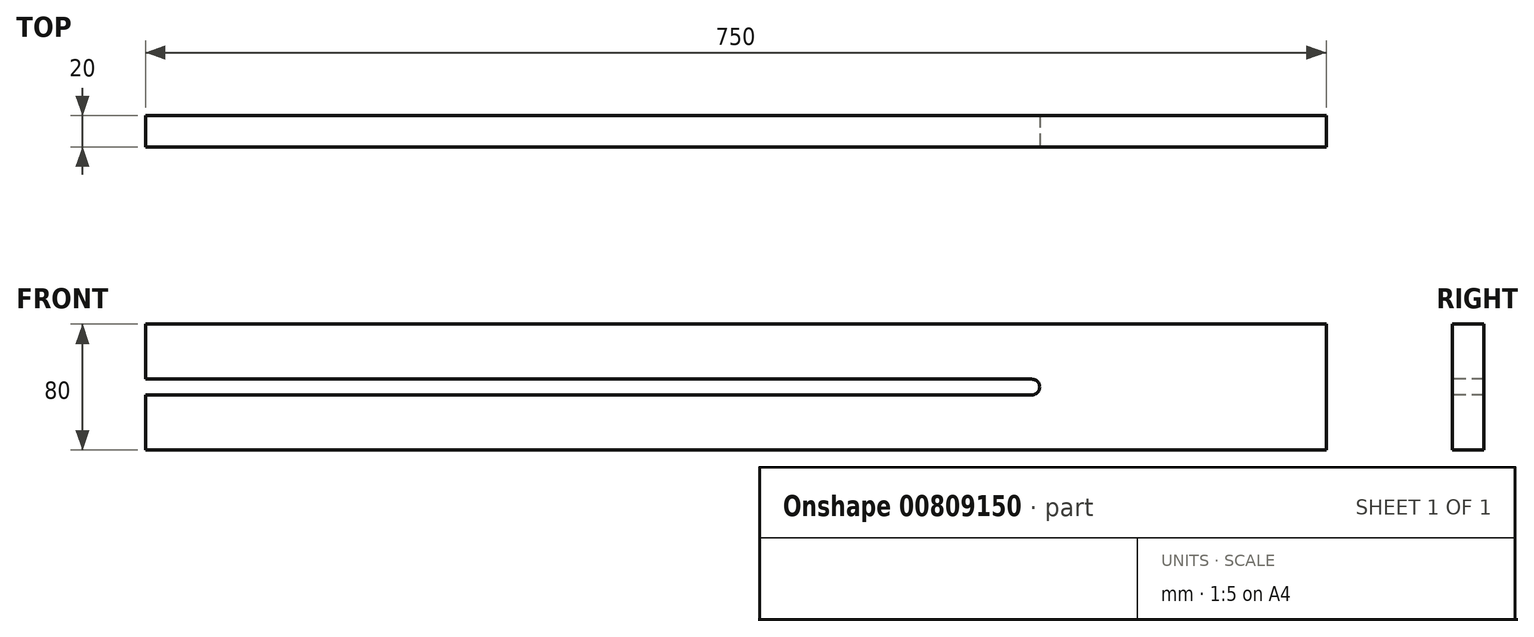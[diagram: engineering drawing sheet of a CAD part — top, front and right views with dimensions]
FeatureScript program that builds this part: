
annotation { "Feature Type Name" : "Feature", "Feature Type Description" : "" }
export const myFeature = defineFeature(function(context is Context, id is Id, definition is map)
    precondition{}
    {
        {
            var Q0;
            Q0=qCreatedBy(makeId("Front.planeOp"),FACE);
            var sketch = newSketch(context, id + "F0", { "sketchPlane" : qUnion([Q0])});
            skLineSegment(sketch, "E0.bottom", {"start": v(375, -40) * mm, "end": v(-375, -40) * mm});
            skLineSegment(sketch, "E0.top", {"start": v(375, 40) * mm, "end": v(-375, 40) * mm});
            skLineSegment(sketch, "E0.left", {"start": v(375, -40) * mm, "end": v(375, 40) * mm});
            skLineSegment(sketch, "E0.right", {"start": v(-375, -40) * mm, "end": v(-375, 40) * mm});
            skPoint(sketch, "E0.middle", {"position": v(0, 0) * mm});
            skSolve(sketch);
        }
        {
            var Q0;
            Q0=makeQuery(id+"F0.imprint","IMPRINT",FACE,{"disambiguationData":[TD([[makeQuery(id+"F0.imprint","IMPRINT",EDGE,{"derivedFrom":sQuery(id+"F0.wireOp",EDGE,"E0.bottom")}),-1.0]])]});
            extrude(context, id + "F1", {"entities" : qUnion([Q0]), "depth" : 20 * mm, "offsetDistance" : 25 * mm});
        }
        {
            var Q0;
            Q0=makeQuery(id+"F1.opExtrude","CAP_FACE",FACE,{"disambiguationData":[OSD([sQuery(id+"F0.wireOp",EDGE,"E0.bottom"),sQuery(id+"F0.wireOp",EDGE,"E0.top"),sQuery(id+"F0.wireOp",EDGE,"E0.left"),sQuery(id+"F0.wireOp",EDGE,"E0.right")])],"isStart":false});
            var sketch = newSketch(context, id + "F2", { "sketchPlane" : qUnion([Q0])});
            skSolve(sketch);
        }
        {
            var Q0;
            Q0=makeQuery(id+"F2.imprint","IMPRINT",FACE,{"disambiguationData":[TD([[makeQuery(id+"F2.imprint","IMPRINT",EDGE,{"derivedFrom":makeQuery(id+"F1.opExtrude","CAP_EDGE",EDGE,{"disambiguationData":[OSD([sQuery(id+"F0.wireOp",EDGE,"E0.bottom")])],"isStart":false})}),-1.0]])]});
            var sketch = newSketch(context, id + "F3", { "sketchPlane" : qUnion([Q0])});
            skLineSegment(sketch, "E1", {"start": v(-375, 5) * mm, "end": v(188, 5) * mm});
            skLineSegment(sketch, "E2", {"start": v(-375, -5) * mm, "end": v(188, -5) * mm});
            skArc(sketch, "E3", {"start": v(188, -5) * mm, "mid": v(193, 0) * mm, "end": v(188, 5) * mm});
            skSolve(sketch);
        }
        {
            var Q0;
            {var subQ0=sQuery(id+"F3.wireOp",EDGE,"E1");Q0=makeQuery(id+"F3.imprint","IMPRINT",FACE,{"disambiguationData":[TD([[makeQuery(id+"F3.imprint","IMPRINT",EDGE,{"derivedFrom":subQ0}),-1.0]])]});}
            extrude(context, id + "F4", {"entities" : qUnion([Q0]), "operationType" : NewBodyOperationType.REMOVE, "endBound" : BoundingType.UP_TO_NEXT, "oppositeDirection" : true, "depth" : 25 * mm, "offsetDistance" : 25 * mm});
        }
    });
